# Revit family: Alcon-13101-MD-M-Revit Family
name_source: partatom
category: Lighting Fixtures
units: mm (PartAtom-declared; Revit-internal decimal feet)

## family parameters
Always vertical = No
Cut with Voids When Loaded = No
Light Source = No
Maintain Annotation Orientation = No
Part Type = Normal
Room Calculation Point = No
Round Connector Dimension = Use Diameter
Shared = No
Work Plane-Based = Yes

## types (1)
- LCALDJ3W-L20UE-DUN-40
    COLOR TEMP = 3000K (90 CRI)
    DIMMING = Non-Dimming (120V)
    Default Elevation = 48"
    Depth = 3 7/16"
    Description = Architectural-grade surface, pendant and track mount adjustable accent LED provides the flexibility to put the light where you want it, whether into tight corners or accenting your favorite sculpture.
    Efficacy = 67 lm/W
    FINISH = W: White
    Height = 7 3/16"
    Housing = White
    IES File = https://www.alconlighting.com
    Instruction Sheet = ETL/cETL listed to UL1598 and UL8750.
    LED = T30:3000K
    Lamp = LED
    Line Art = https://www.alconlighting.com
    Luminous Flux = 2000 lm
    Manufacturer = http://liton.eemagroup.com
    Model = 13301-MD-M
    OPTIONS = Frosted Lens -FR, Louver -LVR
    Photo = https://www.alconlighting.com
    Product Page = https://www.alconlighting.com
    Specification Sheets = https://www.alconlighting.com
    URL = https://www.alconlighting.com
    Wattage = 30 W
    Width = 3 7/16"
    lamp = Lamp

## geometry (parser evidence)
native form markers: Sweep x30
no freeform markers — native parametric forms only
